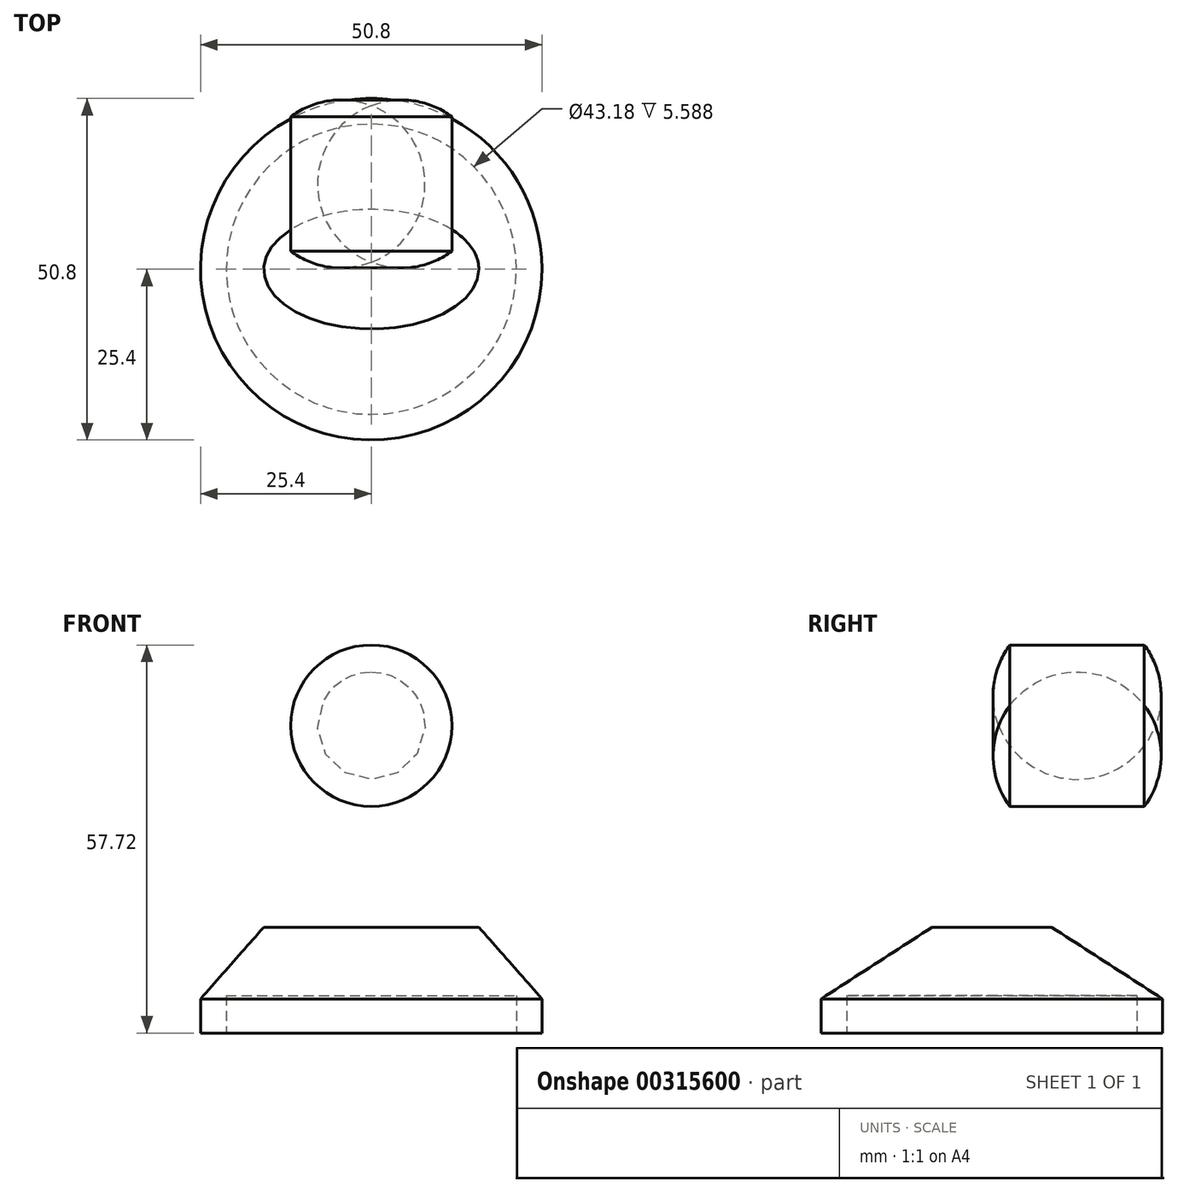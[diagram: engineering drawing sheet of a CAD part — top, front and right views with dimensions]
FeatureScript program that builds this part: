
annotation { "Feature Type Name" : "Feature", "Feature Type Description" : "" }
export const myFeature = defineFeature(function(context is Context, id is Id, definition is map)
    precondition{}
    {
        {
            assignVariable(context, id + "F0", {"name" : "m", "anyValue" : 2});
        }
        {
            var Q0;
            Q0=qCreatedBy(makeId("Front.planeOp"),FACE);
            var sketch = newSketch(context, id + "F1", { "sketchPlane" : qUnion([Q0])});
            skCircle(sketch, "E0", {"center": v(0, 0) * mm, "radius": 17 * mm});
            skCircle(sketch, "E1", {"center": v(0, 0) * mm, "radius": 12 * mm});
            skSolve(sketch);
        }
        {
            var Q0;
            Q0 = qSketchRegion(id + "F1", true);
            extrude(context, id + "F2", {"entities" : qUnion([Q0]), "endBound" : BoundingType.SYMMETRIC, "depth" : getVariable(context, 'm') * 10 * mm});
        }
        {
            var Q0;
            Q0=makeQuery(id+"F2.opExtrude","CAP_EDGE",EDGE,{"disambiguationData":[OSD([sQuery(id+"F1.wireOp",EDGE,"E0")])],"isStart":false});
            var Q1;
            Q1=makeQuery(id+"F2.opExtrude","CAP_EDGE",EDGE,{"disambiguationData":[OSD([sQuery(id+"F1.wireOp",EDGE,"E0")])],"isStart":true});
            fillet(context, id + "F3", {"entities" : qUnion([Q0, Q1]), "radius" : 12.5 * mm, "tangentPropagation" : true, "allowEdgeOverflow" : false});
        }
        {
            var Q0;
            Q0=qCreatedBy(makeId("Top.planeOp"),FACE);
            cPlane(context, id + "F4", {"entities" : qUnion([Q0]), "cplaneType" : CPlaneType.OFFSET, "offset" : getVariable(context, 'm') * 20.32 * mm, "oppositeDirection" : true, "width" : 152.4 * mm, "height" : 152.4 * mm});
        }
        {
            var Q0;
            Q0=qCreatedBy(id+"F4.planeOp",FACE);
            var sketch = newSketch(context, id + "F5", { "sketchPlane" : qUnion([Q0])});
            skCircle(sketch, "E2", {"center": v(0, -12.69) * mm, "radius": 25.4 * mm});
            skSolve(sketch);
        }
        {
            var Q0;
            Q0=qCreatedBy(makeId("Top.planeOp"),FACE);
            cPlane(context, id + "F6", {"entities" : qUnion([Q0]), "cplaneType" : CPlaneType.OFFSET, "offset" : getVariable(context, 'm') * 15 * mm, "oppositeDirection" : true, "width" : 152.4 * mm, "height" : 152.4 * mm});
        }
        {
            var Q0;
            Q0=qCreatedBy(id+"F6.planeOp",FACE);
            var sketch = newSketch(context, id + "F7", { "sketchPlane" : qUnion([Q0])});
            skEllipse(sketch, "E3", {"center": v(0, -12.69) * mm, "majorRadius": 16 * mm, "minorRadius": 8.9 * mm, "majorAxis": v(-1, 0)});
            skSolve(sketch);
        }
        {
            var Q1;
            Q1 = qSketchRegion(id + "F5", true);
            var Q2;
            Q2 = qSketchRegion(id + "F7", true);
            loft(context, id + "F8", {"operationType" : NewBodyOperationType.ADD, "sheetProfilesArray" : [{ "sheetProfileEntities" : qUnion([Q1]) }, { "sheetProfileEntities" : qUnion([Q2]) }]});
        }
        {
            var Q0;
            Q0 = qSketchRegion(id + "F5", true);
            extrude(context, id + "F9", {"entities" : qUnion([Q0]), "operationType" : NewBodyOperationType.ADD, "oppositeDirection" : true, "depth" : getVariable(context, 'm') * 2.54 * mm});
        }
        {
            var Q0;
            Q0=makeQuery(id+"F9.opExtrude","CAP_FACE",FACE,{"disambiguationData":[OSD([sQuery(id+"F5.wireOp",EDGE,"E2")])],"isStart":false});
            var sketch = newSketch(context, id + "F10", { "sketchPlane" : qUnion([Q0])});
            skArc(sketch, "E4", {"start": v(-21.34, 12.69) * mm, "mid": v(0, 34.03) * mm, "end": v(21.34, 12.69) * mm});
            skLineSegment(sketch, "E5", {"start": v(-21.34, 12.69) * mm, "end": v(21.34, 12.69) * mm, "construction": true});
            skArc(sketch, "E6", {"start": v(-16.26, 12.69) * mm, "mid": v(0, 28.95) * mm, "end": v(16.26, 12.69) * mm});
            skLineSegment(sketch, "E7", {"start": v(5.66, 12.69) * mm, "end": v(10.36, 12.69) * mm, "construction": true});
            skLineSegment(sketch, "E8", {"start": v(5.66, 12.69) * mm, "end": v(1.08, 12.69) * mm, "construction": true});
            skLineSegment(sketch, "E9", {"start": v(1.08, 12.69) * mm, "end": v(-31.41, 12.69) * mm, "construction": true});
            skLineSegment(sketch, "E10.MirrorCS", {"start": v(1.08, 12.69) * mm, "end": v(-31.41, 12.69) * mm});
            skLineSegment(sketch, "E11.MirrorCS", {"start": v(5.66, 12.69) * mm, "end": v(1.08, 12.69) * mm});
            skSolve(sketch);
        }
        {
            var Q0;
            Q0=makeQuery(id+"F10.imprint","IMPRINT",FACE,{"disambiguationData":[TD([[makeQuery(id+"F10.imprint","IMPRINT",EDGE,{"derivedFrom":makeQuery(id+"F9.opExtrude","CAP_EDGE",EDGE,{"disambiguationData":[OSD([sQuery(id+"F5.wireOp",EDGE,"E2")])],"isStart":false})}),-1.0]])]});
            var sketch = newSketch(context, id + "F11", { "sketchPlane" : qUnion([Q0])});
            skCircle(sketch, "E12", {"center": v(0, 12.69) * mm, "radius": 21.59 * mm});
            skSolve(sketch);
        }
        {
            var Q0;
            Q0 = qSketchRegion(id + "F11", true);
            extrude(context, id + "F12", {"entities" : qUnion([Q0]), "operationType" : NewBodyOperationType.REMOVE, "oppositeDirection" : true, "depth" : 5.6 * mm});
        }
        {
            var Q0;
            Q0=qCreatedBy(id+"F6.planeOp",FACE);
            cPlane(context, id + "F13", {"entities" : qUnion([Q0]), "cplaneType" : CPlaneType.OFFSET, "offset" : 2.54 * mm, "oppositeDirection" : true, "width" : 152.4 * mm, "height" : 152.4 * mm});
        }
        {
            var Q0;
            Q0=qCreatedBy(id+"F13.planeOp",FACE);
            var sketch = newSketch(context, id + "F14", { "sketchPlane" : qUnion([Q0])});
            skCircle(sketch, "E13", {"center": v(0, -12.69) * mm, "radius": 10.55 * mm});
            skSolve(sketch);
        }
        {
            var Q0;
            Q0 = qSketchRegion(id + "F14", true);
            extrude(context, id + "F15", {"entities" : qUnion([Q0]), "operationType" : NewBodyOperationType.ADD, "oppositeDirection" : true, "depth" : 0.25 * mm});
        }
    });
